# Revit family: CLARK SQUARE 400 SRB
name_source: partatom
category: Plumbing Fixtures
revit_build: Autodesk Revit 2015 (Build: 20140606_1530(x64)
units: mm (PartAtom-declared; Revit-internal decimal feet)

## types (2) — shared parameters
1 Taphole = Yes
Assembly Code = D2010400
CW Connection = No
HW Connection = No
Manufacturer = GWA Bathrooms & Kitchens
Material_Basin = GWA-Porcelain-White
Material_Waste = GWA_Metal-Chrome
Spout Penetration = 80 mm  [stored 0.262467 ft]
URL = https://www.clark.com.au
Vent Connection = No
Waste Connection = Yes
zero-valued in all types: Default Elevation

## per-type parameters (varying)
| type | 3 Tapholes | Model | Tap Penetrations |
| CLARK SQUARE 400 SRB 1TH | No | CL40005-W1 | 5 mm  [stored 0.0164042 ft] |
| CLARK SQUARE 400 SRB 3TH | Yes | CL40005-W3 | 80 mm  [stored 0.262467 ft] |

note: column(s) folded — value = type name in every type: Description

note: [stored X ft] marks values corroborated as IEEE doubles in the binary element streams (Revit-internal decimal feet)

## geometry (parser evidence)
native form markers: Sweep x2
no freeform markers — native parametric forms only
